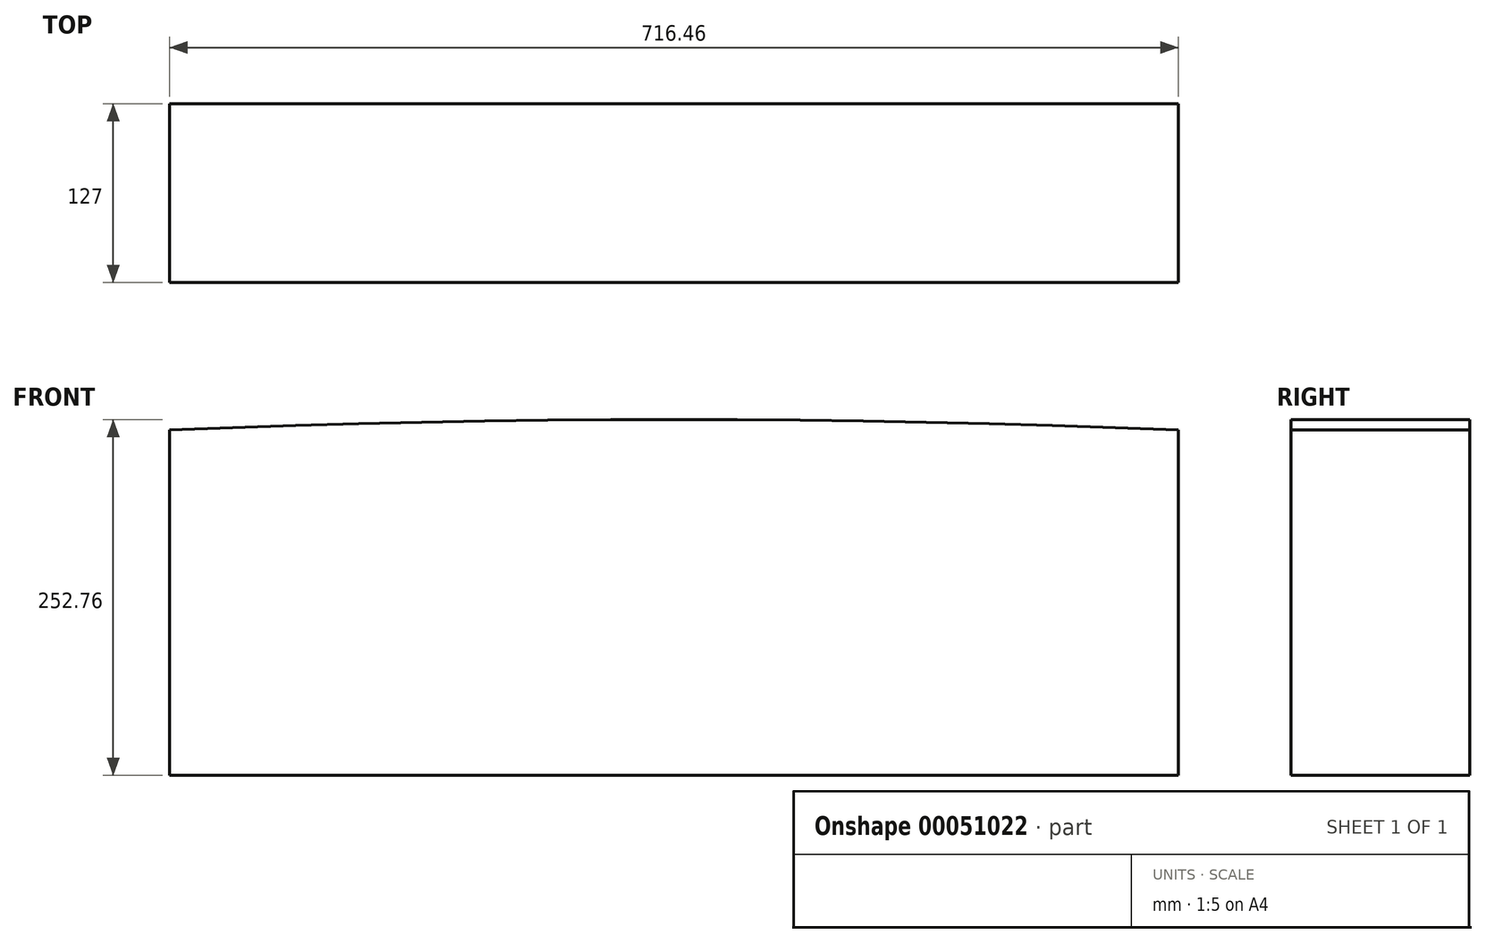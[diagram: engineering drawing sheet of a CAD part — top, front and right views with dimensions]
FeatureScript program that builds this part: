
annotation { "Feature Type Name" : "Feature", "Feature Type Description" : "" }
export const myFeature = defineFeature(function(context is Context, id is Id, definition is map)
    precondition{}
    {
        {
            var Q0;
            Q0=qCreatedBy(makeId("Front.planeOp"),FACE);
            var sketch = newSketch(context, id + "F0", { "sketchPlane" : qUnion([Q0])});
            skLineSegment(sketch, "E0.rect.top", {"start": v(-358.23, -122.67) * mm, "end": v(358.23, -122.67) * mm});
            skLineSegment(sketch, "E0.rect.left", {"start": v(-358.23, 122.67) * mm, "end": v(-358.23, -122.67) * mm});
            skLineSegment(sketch, "E0.rect.right", {"start": v(358.23, 122.67) * mm, "end": v(358.23, -122.67) * mm});
            skPoint(sketch, "E0.rect.middle", {"position": v(0, 0) * mm});
            skArc(sketch, "E1", {"start": v(358.23, 122.67) * mm, "mid": v(0, 130.1) * mm, "end": v(-358.23, 122.67) * mm});
            skSolve(sketch);
        }
        {
            var Q0;
            Q0=makeQuery(id+"F0.imprint","IMPRINT",FACE,{"disambiguationData":[TD([[makeQuery(id+"F0.imprint","IMPRINT",EDGE,{"derivedFrom":sQuery(id+"F0.wireOp",EDGE,"3db684e2-e800-492a-b79b-4ad5f6920f56")}),1.0]])]});
            var Q1;
            Q1=makeQuery(id+"F0.imprint","IMPRINT",FACE,{"disambiguationData":[TD([[makeQuery(id+"F0.imprint","IMPRINT",EDGE,{"derivedFrom":sQuery(id+"F0.wireOp",EDGE,"E0.rect.top")}),1.0]])]});
            extrude(context, id + "F1", {"entities" : qUnion([Q0, Q1]), "depth" : 127 * mm});
        }
    });
